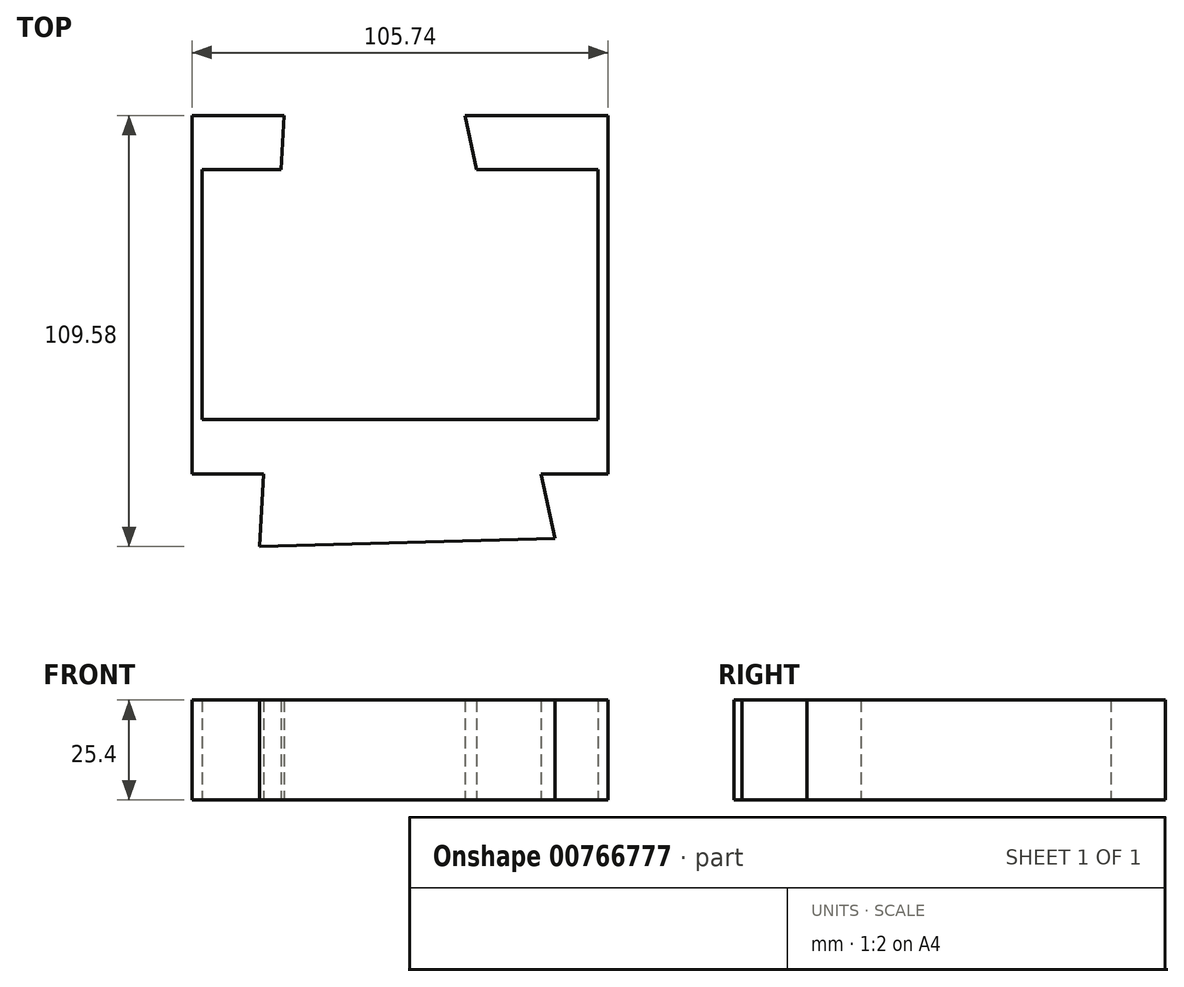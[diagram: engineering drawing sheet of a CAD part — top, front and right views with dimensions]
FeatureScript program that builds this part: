
annotation { "Feature Type Name" : "Feature", "Feature Type Description" : "" }
export const myFeature = defineFeature(function(context is Context, id is Id, definition is map)
    precondition{}
    {
        {
            var Q0;
            Q0=qCreatedBy(makeId("Top.planeOp"),FACE);
            var sketch = newSketch(context, id + "F0", { "sketchPlane" : qUnion([Q0])});
            skLineSegment(sketch, "E0.bottom", {"start": v(50.31, 31.75) * mm, "end": v(19.39, 31.75) * mm});
            skLineSegment(sketch, "E0.top", {"start": v(50.31, -31.75) * mm, "end": v(-50.31, -31.75) * mm});
            skLineSegment(sketch, "E0.left", {"start": v(50.31, 31.75) * mm, "end": v(50.31, -31.75) * mm});
            skLineSegment(sketch, "E0.right", {"start": v(-50.31, 31.75) * mm, "end": v(-50.31, -31.75) * mm});
            skPoint(sketch, "E0.middle", {"position": v(0, 0) * mm});
            skLineSegment(sketch, "E1.bottom", {"start": v(-52.87, 45.57) * mm, "end": v(52.87, 45.57) * mm});
            skLineSegment(sketch, "E1.top", {"start": v(-52.87, -45.57) * mm, "end": v(-34.66, -45.57) * mm});
            skLineSegment(sketch, "E1.left", {"start": v(-52.87, 45.57) * mm, "end": v(-52.87, -45.57) * mm});
            skLineSegment(sketch, "E1.right", {"start": v(52.87, 45.57) * mm, "end": v(52.87, -45.57) * mm});
            skLineSegment(sketch, "E2", {"start": v(-29.46, 45.57) * mm, "end": v(-30.25, 31.75) * mm});
            skLineSegment(sketch, "E3", {"start": v(-35.72, -64) * mm, "end": v(39.3, -61.96) * mm});
            skLineSegment(sketch, "E4", {"start": v(39.3, -61.96) * mm, "end": v(35.82, -45.57) * mm});
            skLineSegment(sketch, "E5.trimOffspring", {"start": v(-30.25, 31.75) * mm, "end": v(-50.31, 31.75) * mm});
            skLineSegment(sketch, "E6.trimOffspring", {"start": v(-34.66, -45.57) * mm, "end": v(-35.72, -64) * mm});
            skLineSegment(sketch, "E7.trimOffspring", {"start": v(35.82, -45.57) * mm, "end": v(52.87, -45.57) * mm});
            skLineSegment(sketch, "E8.trimOffspring", {"start": v(19.39, 31.75) * mm, "end": v(16.45, 45.57) * mm});
            skSolve(sketch);
        }
        {
            var Q0;
            Q0=makeQuery(id+"F0.imprint","IMPRINT",FACE,{"disambiguationData":[TD([[makeQuery(id+"F0.imprint","IMPRINT",EDGE,{"derivedFrom":sQuery(id+"F0.wireOp",EDGE,"E0.bottom")}),-1.0]])]});
            extrude(context, id + "F1", {"entities" : qUnion([Q0]), "depth" : 25.4 * mm, "offsetDistance" : 25.4 * mm});
        }
    });
